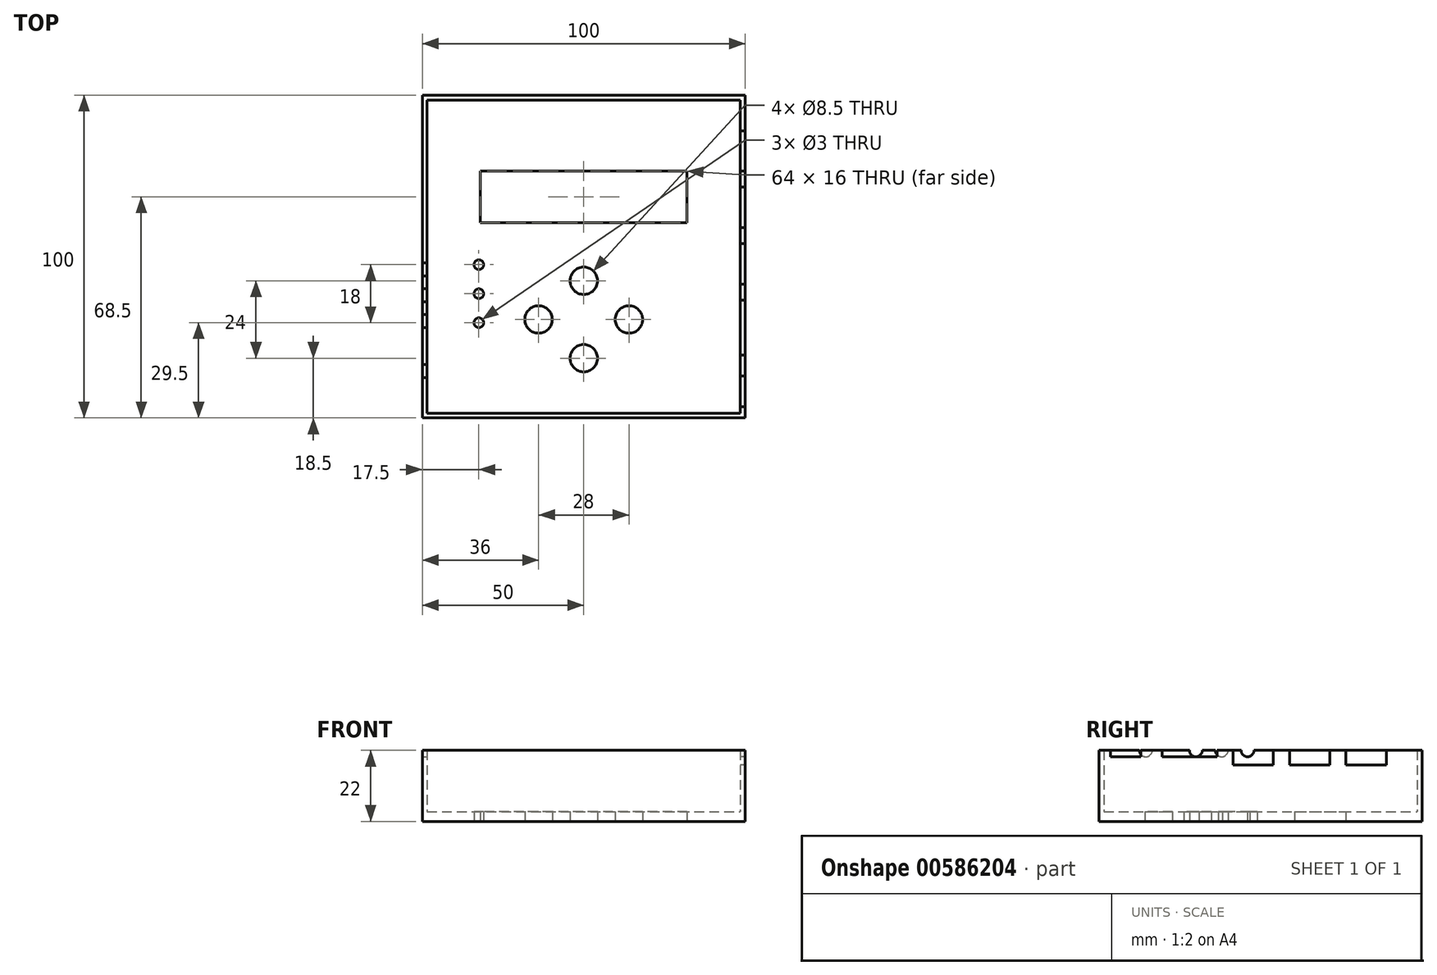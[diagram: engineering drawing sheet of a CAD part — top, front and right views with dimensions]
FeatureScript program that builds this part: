
annotation { "Feature Type Name" : "Feature", "Feature Type Description" : "" }
export const myFeature = defineFeature(function(context is Context, id is Id, definition is map)
    precondition{}
    {
        {
            var Q0;
            Q0=qCreatedBy(makeId("Top.planeOp"),FACE);
            var sketch = newSketch(context, id + "F0", { "sketchPlane" : qUnion([Q0])});
            skLineSegment(sketch, "E0.bottom", {"start": v(-50, 50) * mm, "end": v(50, 50) * mm});
            skLineSegment(sketch, "E0.top", {"start": v(-50, -50) * mm, "end": v(50, -50) * mm});
            skLineSegment(sketch, "E0.left", {"start": v(-50, 50) * mm, "end": v(-50, -50) * mm});
            skLineSegment(sketch, "E0.right", {"start": v(50, 50) * mm, "end": v(50, -50) * mm});
            skPoint(sketch, "E0.middle", {"position": v(0, 0) * mm});
            skLineSegment(sketch, "E1.bottom", {"start": v(-48.5, -48.5) * mm, "end": v(48.5, -48.5) * mm});
            skLineSegment(sketch, "E1.top", {"start": v(-48.5, 48.5) * mm, "end": v(48.5, 48.5) * mm});
            skLineSegment(sketch, "E1.left", {"start": v(-48.5, -48.5) * mm, "end": v(-48.5, 48.5) * mm});
            skLineSegment(sketch, "E1.right", {"start": v(48.5, -48.5) * mm, "end": v(48.5, 48.5) * mm});
            skLineSegment(sketch, "E2.bottom", {"start": v(32, 10.5) * mm, "end": v(-32, 10.5) * mm});
            skLineSegment(sketch, "E2.top", {"start": v(32, 26.5) * mm, "end": v(-32, 26.5) * mm});
            skLineSegment(sketch, "E2.left", {"start": v(32, 10.5) * mm, "end": v(32, 26.5) * mm});
            skLineSegment(sketch, "E2.right", {"start": v(-32, 10.5) * mm, "end": v(-32, 26.5) * mm});
            skPoint(sketch, "E2.middle", {"position": v(0, 18.5) * mm});
            skCircle(sketch, "E3", {"center": v(-32.5, -2.5) * mm, "radius": 1.5 * mm});
            skCircle(sketch, "E4", {"center": v(-32.5, -11.5) * mm, "radius": 1.5 * mm});
            skCircle(sketch, "E5", {"center": v(-32.5, -20.5) * mm, "radius": 1.5 * mm});
            skCircle(sketch, "E6", {"center": v(0, -7.5) * mm, "radius": 4.25 * mm});
            skCircle(sketch, "E7", {"center": v(0, -31.5) * mm, "radius": 4.25 * mm});
            skCircle(sketch, "E8", {"center": v(14, -19.5) * mm, "radius": 4.25 * mm});
            skLineSegment(sketch, "E9", {"start": v(0, 48.5) * mm, "end": v(0, -48.5) * mm});
            skCircle(sketch, "E10", {"center": v(-14, -19.5) * mm, "radius": 4.25 * mm});
            skLineSegment(sketch, "E11.MirrorCS", {"start": v(0, -125.23) * mm, "end": v(0, -28.23) * mm});
            skSolve(sketch);
        }
        {
            var Q0;
            {var subQ13=sQuery(id+"F0.wireOp",EDGE,"E1.left");Q0=makeQuery(id+"F0.imprint","IMPRINT",FACE,{"disambiguationData":[TD([[makeQuery(id+"F0.imprint","IMPRINT",EDGE,{"derivedFrom":subQ13}),-1.0]])]});}
            var Q1;
            {var subQ4=sQuery(id+"F0.wireOp",EDGE,"E1.right");Q1=makeQuery(id+"F0.imprint","IMPRINT",FACE,{"disambiguationData":[TD([[makeQuery(id+"F0.imprint","IMPRINT",EDGE,{"derivedFrom":subQ4}),1.0]])]});}
            extrude(context, id + "F1", {"entities" : qUnion([Q0, Q1]), "depth" : 3 * mm, "offsetDistance" : 25 * mm});
        }
        {
            var Q0;
            Q0=makeQuery(id+"F0.imprint","IMPRINT",FACE,{"disambiguationData":[TD([[makeQuery(id+"F0.imprint","IMPRINT",EDGE,{"derivedFrom":sQuery(id+"F0.wireOp",EDGE,"E0.bottom")}),-1.0]])]});
            extrude(context, id + "F2", {"entities" : qUnion([Q0]), "operationType" : NewBodyOperationType.ADD, "depth" : 22 * mm, "offsetDistance" : 25 * mm});
        }
        {
            var Q0;
            Q0=qCreatedBy(makeId("Right.planeOp"),FACE);
            var sketch = newSketch(context, id + "F3", { "sketchPlane" : qUnion([Q0])});
            skLineSegment(sketch, "E12.bottom", {"start": v(-46.5, 31) * mm, "end": v(-37, 31) * mm});
            skLineSegment(sketch, "E12.top", {"start": v(-46.5, 20) * mm, "end": v(-37, 20) * mm});
            skLineSegment(sketch, "E12.left", {"start": v(-46.5, 31) * mm, "end": v(-46.5, 20) * mm});
            skLineSegment(sketch, "E12.right", {"start": v(-37, 31) * mm, "end": v(-37, 20) * mm});
            skSolve(sketch);
        }
        {
            var Q0;
            Q0=makeQuery(id+"F3.imprint","IMPRINT",FACE,{"disambiguationData":[TD([[makeQuery(id+"F3.imprint","IMPRINT",EDGE,{"derivedFrom":sQuery(id+"F3.wireOp",EDGE,"E12.bottom")}),-1.0]])]});
            var Q1;
            Q1=makeQuery(id+"F2.opExtrude","SWEPT_FACE",FACE,{"disambiguationData":[OSD([sQuery(id+"F0.wireOp",EDGE,"E0.right")])]});
            var Q2;
            Q2=makeQuery(id+"F11.opExtrude","SWEPT_BODY",BODY,{"disambiguationData":[OSD([sQuery(id+"F0.wireOp",EDGE,"E0.bottom")])]});
            extrude(context, id + "F4", {"entities" : qUnion([Q0, Q1]), "operationType" : NewBodyOperationType.REMOVE, "endBound" : BoundingType.THROUGH_ALL, "depth" : 59.3 * mm, "endBoundEntityBody" : qUnion([Q2]), "offsetDistance" : 25 * mm});
        }
        {
            var Q0;
            Q0=qCreatedBy(makeId("Right.planeOp"),FACE);
            var sketch = newSketch(context, id + "F5", { "sketchPlane" : qUnion([Q0])});
            skLineSegment(sketch, "E13.bottom", {"start": v(-30.5, 23.33) * mm, "end": v(-13.5, 23.33) * mm});
            skLineSegment(sketch, "E13.top", {"start": v(-30.5, 20) * mm, "end": v(-13.5, 20) * mm});
            skLineSegment(sketch, "E13.left", {"start": v(-30.5, 23.33) * mm, "end": v(-30.5, 20) * mm});
            skLineSegment(sketch, "E13.right", {"start": v(-13.5, 23.33) * mm, "end": v(-13.5, 20) * mm});
            skSolve(sketch);
        }
        {
            var Q0;
            Q0=makeQuery(id+"F5.imprint","IMPRINT",FACE,{"disambiguationData":[TD([[makeQuery(id+"F5.imprint","IMPRINT",EDGE,{"derivedFrom":sQuery(id+"F5.wireOp",EDGE,"E13.bottom")}),-1.0]])]});
            extrude(context, id + "F6", {"entities" : qUnion([Q0]), "operationType" : NewBodyOperationType.REMOVE, "depth" : 76.9 * mm, "offsetDistance" : 25 * mm});
        }
        {
            var Q0;
            Q0=qCreatedBy(makeId("Right.planeOp"),FACE);
            var sketch = newSketch(context, id + "F7", { "sketchPlane" : qUnion([Q0])});
            skLineSegment(sketch, "E14.bottom", {"start": v(-8.5, 26.05) * mm, "end": v(4, 26.05) * mm});
            skLineSegment(sketch, "E14.top", {"start": v(-8.5, 17.5) * mm, "end": v(4, 17.5) * mm});
            skLineSegment(sketch, "E14.left", {"start": v(-8.5, 26.05) * mm, "end": v(-8.5, 17.5) * mm});
            skLineSegment(sketch, "E14.right", {"start": v(4, 26.05) * mm, "end": v(4, 17.5) * mm});
            skLineSegment(sketch, "E15.bottom", {"start": v(9, 25.84) * mm, "end": v(21.5, 25.84) * mm});
            skLineSegment(sketch, "E15.top", {"start": v(9, 17.5) * mm, "end": v(21.5, 17.5) * mm});
            skLineSegment(sketch, "E15.left", {"start": v(9, 25.84) * mm, "end": v(9, 17.5) * mm});
            skLineSegment(sketch, "E15.right", {"start": v(21.5, 25.84) * mm, "end": v(21.5, 17.5) * mm});
            skLineSegment(sketch, "E16.bottom", {"start": v(26.5, 25.71) * mm, "end": v(39, 25.71) * mm});
            skLineSegment(sketch, "E16.top", {"start": v(26.5, 17.5) * mm, "end": v(39, 17.5) * mm});
            skLineSegment(sketch, "E16.left", {"start": v(26.5, 25.71) * mm, "end": v(26.5, 17.5) * mm});
            skLineSegment(sketch, "E16.right", {"start": v(39, 25.71) * mm, "end": v(39, 17.5) * mm});
            skSolve(sketch);
        }
        {
            var Q0;
            Q0=makeQuery(id+"F7.imprint","IMPRINT",FACE,{"disambiguationData":[TD([[makeQuery(id+"F7.imprint","IMPRINT",EDGE,{"derivedFrom":sQuery(id+"F7.wireOp",EDGE,"E16.bottom")}),-1.0]])]});
            var Q1;
            Q1=makeQuery(id+"F7.imprint","IMPRINT",FACE,{"disambiguationData":[TD([[makeQuery(id+"F7.imprint","IMPRINT",EDGE,{"derivedFrom":sQuery(id+"F7.wireOp",EDGE,"E15.bottom")}),-1.0]])]});
            var Q2;
            Q2=makeQuery(id+"F7.imprint","IMPRINT",FACE,{"disambiguationData":[TD([[makeQuery(id+"F7.imprint","IMPRINT",EDGE,{"derivedFrom":sQuery(id+"F7.wireOp",EDGE,"E14.bottom")}),-1.0]])]});
            extrude(context, id + "F8", {"entities" : qUnion([Q0, Q1, Q2]), "operationType" : NewBodyOperationType.REMOVE, "depth" : 63.2 * mm, "offsetDistance" : 25 * mm});
        }
        {
            var Q0;
            Q0=qCreatedBy(makeId("Right.planeOp"),FACE);
            var sketch = newSketch(context, id + "F9", { "sketchPlane" : qUnion([Q0])});
            skCircle(sketch, "E17", {"center": v(-4, 22) * mm, "radius": 2 * mm});
            skCircle(sketch, "E18", {"center": v(-35.5, 22) * mm, "radius": 2 * mm});
            skCircle(sketch, "E19", {"center": v(-20, 22) * mm, "radius": 2 * mm});
            skCircle(sketch, "E20", {"center": v(-12, 22) * mm, "radius": 2 * mm});
            skSolve(sketch);
        }
        {
            var Q0;
            Q0=makeQuery(id+"F9.imprint","IMPRINT",FACE,{"disambiguationData":[TD([[makeQuery(id+"F9.imprint","IMPRINT",EDGE,{"derivedFrom":sQuery(id+"F9.wireOp",EDGE,"E20")}),1.0]])]});
            var Q1;
            Q1=makeQuery(id+"F9.imprint","IMPRINT",FACE,{"disambiguationData":[TD([[makeQuery(id+"F9.imprint","IMPRINT",EDGE,{"derivedFrom":sQuery(id+"F9.wireOp",EDGE,"E17")}),1.0]])]});
            var Q2;
            Q2=makeQuery(id+"F9.imprint","IMPRINT",FACE,{"disambiguationData":[TD([[makeQuery(id+"F9.imprint","IMPRINT",EDGE,{"derivedFrom":sQuery(id+"F9.wireOp",EDGE,"E19")}),1.0]])]});
            var Q3;
            Q3=makeQuery(id+"F9.imprint","IMPRINT",FACE,{"disambiguationData":[TD([[makeQuery(id+"F9.imprint","IMPRINT",EDGE,{"derivedFrom":sQuery(id+"F9.wireOp",EDGE,"E18")}),1.0]])]});
            extrude(context, id + "F10", {"entities" : qUnion([Q0, Q1, Q2, Q3]), "operationType" : NewBodyOperationType.REMOVE, "oppositeDirection" : true, "depth" : 67.3 * mm, "offsetDistance" : 25 * mm});
        }
        {
            var Q0;
            Q0=sQuery(id+"F0.wireOp",EDGE,"E0.left");
            var Q1;
            Q1=sQuery(id+"F0.wireOp",EDGE,"E1.left");
            var Q2;
            Q2=sQuery(id+"F0.wireOp",EDGE,"E1.top");
            var Q3;
            Q3=sQuery(id+"F0.wireOp",EDGE,"E0.bottom");
            var Q4;
            Q4=sQuery(id+"F0.wireOp",EDGE,"E0.right");
            var Q5;
            Q5=sQuery(id+"F0.wireOp",EDGE,"E1.right");
            var Q6;
            Q6=sQuery(id+"F0.wireOp",EDGE,"E1.bottom");
            var Q7;
            Q7=sQuery(id+"F0.wireOp",EDGE,"E0.top");
            extrude(context, id + "F11", {"bodyType" : ToolBodyType.SURFACE, "surfaceEntities" : qUnion([Q0, Q1, Q2, Q3, Q4, Q5, Q6, Q7]), "depth" : 22 * mm, "offsetDistance" : 25 * mm});
        }
        {
            var Q0;
            Q0=makeQuery(id+"F11.opExtrude","SWEPT_EDGE",EDGE,{"disambiguationData":[OSD([sQuery(id+"F0.wireOp",VERTEX,"E0.bottom.start")])]});
            var Q1;
            Q1=makeQuery(id+"F11.opExtrude","SWEPT_EDGE",EDGE,{"disambiguationData":[OSD([sQuery(id+"F0.wireOp",VERTEX,"E0.right.start")])]});
            var Q2;
            Q2=makeQuery(id+"F11.opExtrude","SWEPT_EDGE",EDGE,{"disambiguationData":[OSD([sQuery(id+"F0.wireOp",VERTEX,"E0.top.end")])]});
            var Q3;
            Q3=makeQuery(id+"F11.opExtrude","SWEPT_EDGE",EDGE,{"disambiguationData":[OSD([sQuery(id+"F0.wireOp",VERTEX,"E0.top.start")])]});
            fillet(context, id + "F12", {"entities" : qUnion([Q0, Q1, Q2, Q3]), "radius" : 1.6 * mm, "tangentPropagation" : true, "rho" : 0.5, "crossSection" : FilletCrossSection.CONIC, "allowEdgeOverflow" : false});
        }
    });
